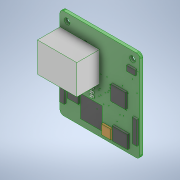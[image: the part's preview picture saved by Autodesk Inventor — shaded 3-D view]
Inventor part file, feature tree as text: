
AUTODESK INVENTOR PART (.ipt)
format: ipt  version: 2020 (Build 240168000, 168)  size: 391,680 bytes
history: native  units: in
note: dims shown in document units (in); Inventor stores cm internally (conversion verified against a paired STEP export)
features: extrude x13, other x11, sketch x1
ambient origin geometry x8: Origin, YZ Plane, XZ Plane, XY Plane, X Axis, Y Axis, Z Axis, Center Point
bodies: Solid1 (feature_tree)
feature tree (25):
  extrude  "ethernet_poe.brd_Outline"  Depth=0.063in
  extrude  "C20_2"  Depth=0.0394in TaperAngle=0.0deg
  extrude  "D2_4"  Depth=0.0394in TaperAngle=0.0deg
  extrude  "D3_6"  Depth=0.0394in TaperAngle=0.0deg
  extrude  "D4_8"  Depth=0.0394in TaperAngle=0.0deg
  extrude  "J1_10"  Depth=0.4921in TaperAngle=0.0deg
  extrude  "J2_12"  Depth=0.0394in TaperAngle=0.0deg
  extrude  "J3_14"  Depth=0.0394in TaperAngle=0.0deg
  extrude  "UH_16"  Depth=0.0004in TaperAngle=0.0deg
  extrude  "S1_18"  Depth=0.0394in TaperAngle=0.0deg
  extrude  "U1_22"  Depth=0.0394in TaperAngle=0.0deg
  extrude  "U2_24"  Depth=0.0394in TaperAngle=0.0deg
  extrude  "U3_26"  Depth=0.0394in TaperAngle=0.0deg
  sketch  "Sketch1"  dims[d0=0.063in d1=0.0in d2=0.063in d3=0.0394in d4=0.0in d5=0.0394in d6=0.0in d7=0.0394in d8=0.0in d9=0.0394in d10=0.0in d11=0.4921in d12=0.0in d13=0.0394in d14=0.0in d15=0.0394in d16=0.0in d17=0.0004in d18=0.0in d19=0.0394in d20=0.0in d23=0.0394in d24=0.0in d25=0.0394in d26=0.0in d27=0.0394in d28=0.0in]
  other  "E2-5, E2-5_1"
  other  "CHIP-LED0603, CHIP-LED0603_3"
  other  "CHIP-LED0603, CHIP-LED0603_5"
  other  "CHIP-LED0603, CHIP-LED0603_7"
  other  "ARJP11A-MBSB-A-B-EMU2, ARJP11A_9"
  other  "1X05, J2_1X05_11"
  other  "1X05, J3_1X05_13"
  other  "KMR2, KMR2_17"
  other  "48-LQFP, W5500_21"
  other  "SOIC-8-EXPOSED_PAD, IFX91041_23"
  other  "SOT230P700X180-4N, AZ1117EH-3_3TRG1_25"
